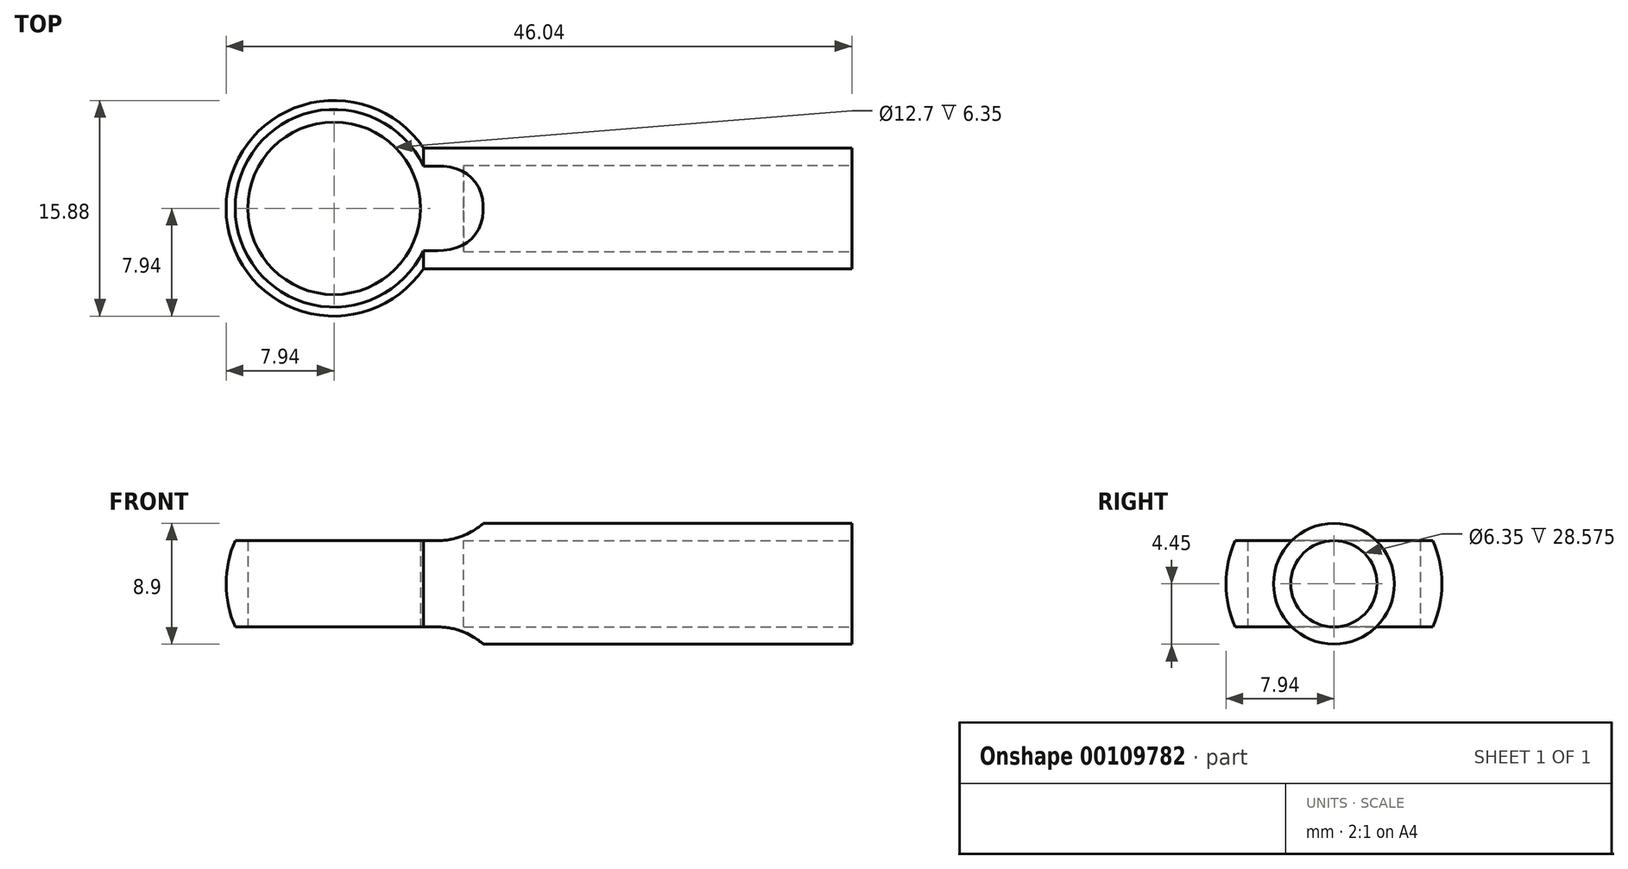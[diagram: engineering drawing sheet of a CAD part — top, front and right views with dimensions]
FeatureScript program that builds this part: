
annotation { "Feature Type Name" : "Feature", "Feature Type Description" : "" }
export const myFeature = defineFeature(function(context is Context, id is Id, definition is map)
    precondition{}
    {
        {
            var Q0;
            Q0=qCreatedBy(makeId("Front.planeOp"),FACE);
            var sketch = newSketch(context, id + "F0", { "sketchPlane" : qUnion([Q0])});
            skLineSegment(sketch, "E0", {"start": v(0, 0) * mm, "end": v(358.78, 0) * mm, "construction": true});
            skCircle(sketch, "E1", {"center": v(358.78, 0) * mm, "radius": 3.18 * mm});
            skCircle(sketch, "E2", {"center": v(358.78, 0) * mm, "radius": 4.76 * mm});
            skArc(sketch, "E3", {"start": v(0, -7.94) * mm, "mid": v(7.94, 0) * mm, "end": v(0, 7.94) * mm});
            skLineSegment(sketch, "E4", {"start": v(38.1, 0) * mm, "end": v(38.1, -4.45) * mm});
            skLineSegment(sketch, "E5", {"start": v(38.1, -4.45) * mm, "end": v(6.58, -4.45) * mm});
            skLineSegment(sketch, "E6", {"start": v(0, 7.94) * mm, "end": v(0, -7.94) * mm});
            skLineSegment(sketch, "E7", {"start": v(7.94, 0) * mm, "end": v(38.1, 0) * mm});
            skPoint(sketch, "E8.orphan", {"position": v(38.1, 4.45) * mm});
            skSolve(sketch);
        }
        {
            var Q0;
            Q0=qCreatedBy(makeId("Top.planeOp"),FACE);
            var sketch = newSketch(context, id + "F1", { "sketchPlane" : qUnion([Q0])});
            skCircle(sketch, "E9", {"center": v(0, 0) * mm, "radius": 19.85 * mm});
            skSolve(sketch);
        }
        {
            var Q0;
            {var subQ0=sQuery(id+"F0.wireOp",EDGE,"E6");Q0=makeQuery(id+"F0.imprint","IMPRINT",FACE,{"disambiguationData":[TD([[makeQuery(id+"F0.imprint","IMPRINT",EDGE,{"derivedFrom":subQ0}),1.0]])]});}
            var Q1;
            Q1=sQuery(id+"F1.wireOp",EDGE,"E9");
            sweep(context, id + "F2", {"profiles" : qUnion([Q0]), "path" : qUnion([Q1])});
        }
        {
            var Q0;
            Q0=qCreatedBy(makeId("Right.planeOp"),FACE);
            var sketch = newSketch(context, id + "F3", { "sketchPlane" : qUnion([Q0])});
            skCircle(sketch, "E10", {"center": v(0, 0) * mm, "radius": 17.63 * mm});
            skSolve(sketch);
        }
        {
            var Q0;
            Q0=makeQuery(id+"F0.imprint","IMPRINT",FACE,{"disambiguationData":[TD([[makeQuery(id+"F0.imprint","IMPRINT",EDGE,{"derivedFrom":sQuery(id+"F0.wireOp",EDGE,"E4")}),-1.0]])]});
            var Q1;
            Q1=sQuery(id+"F3.wireOp",EDGE,"E10");
            sweep(context, id + "F4", {"operationType" : NewBodyOperationType.ADD, "profiles" : qUnion([Q0]), "path" : qUnion([Q1])});
        }
        {
            var Q0;
            Q0=makeQuery(id+"F4.opSweep","SWEPT_FACE",FACE,{"disambiguationData":[OSD([sQuery(id+"F0.wireOp",EDGE,"E4"),sQuery(id+"F3.wireOp",EDGE,"E10")])]});
            var sketch = newSketch(context, id + "F5", { "sketchPlane" : qUnion([Q0])});
            skCircle(sketch, "E11", {"center": v(0, 0) * mm, "radius": 3.18 * mm});
            skSolve(sketch);
        }
        {
            var Q0;
            Q0 = qSketchRegion(id + "F5", true);
            extrude(context, id + "F6", {"entities" : qUnion([Q0]), "operationType" : NewBodyOperationType.REMOVE, "oppositeDirection" : true, "depth" : 28.57 * mm});
        }
        {
            var Q0;
            Q0=qCreatedBy(makeId("Front.planeOp"),FACE);
            var sketch = newSketch(context, id + "F7", { "sketchPlane" : qUnion([Q0])});
            skLineSegment(sketch, "E12", {"start": v(-12.94, 3.18) * mm, "end": v(7.62, 3.18) * mm});
            skLineSegment(sketch, "E13", {"start": v(12.7, 8.26) * mm, "end": v(12.7, 8.26) * mm});
            skLineSegment(sketch, "E14", {"start": v(12.7, 8.26) * mm, "end": v(-13.07, 8.26) * mm});
            skLineSegment(sketch, "E15", {"start": v(-13.07, 8.26) * mm, "end": v(-12.94, 3.17) * mm});
            skPoint(sketch, "E16.visualSharp", {"position": v(12.7, 3.18) * mm});
            skArc(sketch, "E16.filletArc", {"start": v(7.62, 3.18) * mm, "mid": v(11.21, 4.66) * mm, "end": v(12.7, 8.26) * mm});
            skLineSegment(sketch, "E17.MirrorCS", {"start": v(12.7, -8.26) * mm, "end": v(-13.07, -8.26) * mm});
            skLineSegment(sketch, "E18.MirrorCS", {"start": v(-13.07, -8.26) * mm, "end": v(-12.94, -3.17) * mm});
            skLineSegment(sketch, "E19.MirrorCS", {"start": v(12.7, -8.26) * mm, "end": v(12.7, -8.26) * mm});
            skArc(sketch, "E20.MirrorCS", {"start": v(7.62, -3.18) * mm, "mid": v(11.21, -4.66) * mm, "end": v(12.7, -8.26) * mm});
            skLineSegment(sketch, "E21.MirrorCS", {"start": v(-12.94, -3.18) * mm, "end": v(7.62, -3.18) * mm});
            skSolve(sketch);
        }
        {
            var Q0;
            Q0 = qSketchRegion(id + "F7", true);
            extrude(context, id + "F8", {"entities" : qUnion([Q0]), "operationType" : NewBodyOperationType.REMOVE, "endBound" : BoundingType.SYMMETRIC, "depth" : 25.4 * mm});
        }
        {
            var Q0;
            Q0=makeQuery(id+"F8.boolean.opBoolean","COPY",FACE,{"derivedFrom":makeQuery(id+"F8.opExtrude","SWEPT_FACE",FACE,{"disambiguationData":[OSD([sQuery(id+"F7.wireOp",EDGE,"E12")])]})});
            var sketch = newSketch(context, id + "F9", { "sketchPlane" : qUnion([Q0])});
            skCircle(sketch, "E22", {"center": v(0, 0) * mm, "radius": 6.35 * mm});
            skSolve(sketch);
        }
        {
            var Q0;
            Q0 = qSketchRegion(id + "F9", true);
            extrude(context, id + "F10", {"entities" : qUnion([Q0]), "operationType" : NewBodyOperationType.REMOVE, "endBound" : BoundingType.SYMMETRIC, "depth" : 25.4 * mm});
        }
    });
